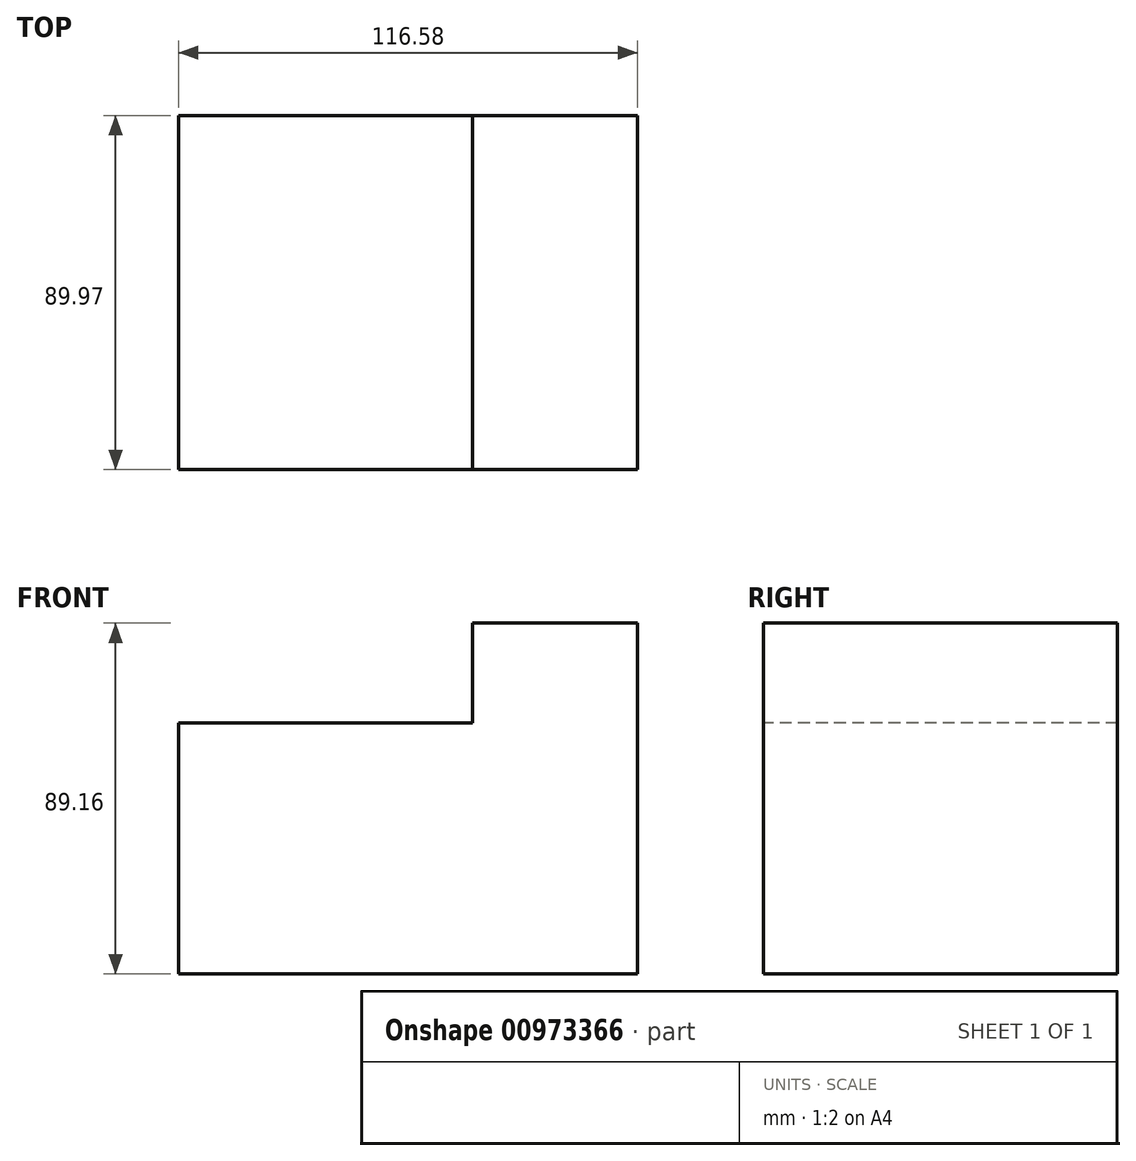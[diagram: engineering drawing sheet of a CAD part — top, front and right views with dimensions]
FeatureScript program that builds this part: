
annotation { "Feature Type Name" : "Feature", "Feature Type Description" : "" }
export const myFeature = defineFeature(function(context is Context, id is Id, definition is map)
    precondition{}
    {
        {
            var Q0;
            Q0=qCreatedBy(makeId("Top.planeOp"),FACE);
            var sketch = newSketch(context, id + "F0", { "sketchPlane" : qUnion([Q0])});
            skLineSegment(sketch, "E0.bottom", {"start": v(-50.21, 43.16) * mm, "end": v(66.37, 43.16) * mm});
            skLineSegment(sketch, "E0.top", {"start": v(-50.21, -46.81) * mm, "end": v(66.37, -46.81) * mm});
            skLineSegment(sketch, "E0.left", {"start": v(-50.21, 43.16) * mm, "end": v(-50.21, -46.81) * mm});
            skLineSegment(sketch, "E0.right", {"start": v(66.37, 43.16) * mm, "end": v(66.37, -46.81) * mm});
            skSolve(sketch);
        }
        {
            var Q0;
            Q0=makeQuery(id+"F0.imprint","IMPRINT",FACE,{"disambiguationData":[TD([[makeQuery(id+"F0.imprint","IMPRINT",EDGE,{"derivedFrom":sQuery(id+"F0.wireOp",EDGE,"E0.bottom")}),-1.0]])]});
            extrude(context, id + "F1", {"entities" : qUnion([Q0]), "depth" : 63.76 * mm, "offsetDistance" : 25.4 * mm});
        }
        {
            var Q0;
            Q0=makeQuery(id+"F1.opExtrude","CAP_FACE",FACE,{"disambiguationData":[OSD([sQuery(id+"F0.wireOp",EDGE,"E0.bottom"),sQuery(id+"F0.wireOp",EDGE,"E0.top"),sQuery(id+"F0.wireOp",EDGE,"E0.left"),sQuery(id+"F0.wireOp",EDGE,"E0.right")])],"isStart":false});
            var sketch = newSketch(context, id + "F2", { "sketchPlane" : qUnion([Q0])});
            skLineSegment(sketch, "E1", {"start": v(24.48, 43.16) * mm, "end": v(24.48, -46.81) * mm});
            skLineSegment(sketch, "E2", {"start": v(47.62, 43.16) * mm, "end": v(47.62, -46.81) * mm});
            skSolve(sketch);
        }
        {
            var Q0;
            {var subQ0=sQuery(id+"F2.wireOp",EDGE,"E1");Q0=makeQuery(id+"F2.imprint","IMPRINT",FACE,{"disambiguationData":[TD([[makeQuery(id+"F2.imprint","IMPRINT",EDGE,{"derivedFrom":subQ0}),1.0]])]});}
            var Q1;
            {var subQ0=sQuery(id+"F2.wireOp",EDGE,"E2");Q1=makeQuery(id+"F2.imprint","IMPRINT",FACE,{"disambiguationData":[TD([[makeQuery(id+"F2.imprint","IMPRINT",EDGE,{"derivedFrom":subQ0}),1.0]])]});}
            extrude(context, id + "F3", {"entities" : qUnion([Q0, Q1]), "operationType" : NewBodyOperationType.ADD, "depth" : 25.4 * mm, "offsetDistance" : 25.4 * mm});
        }
    });
